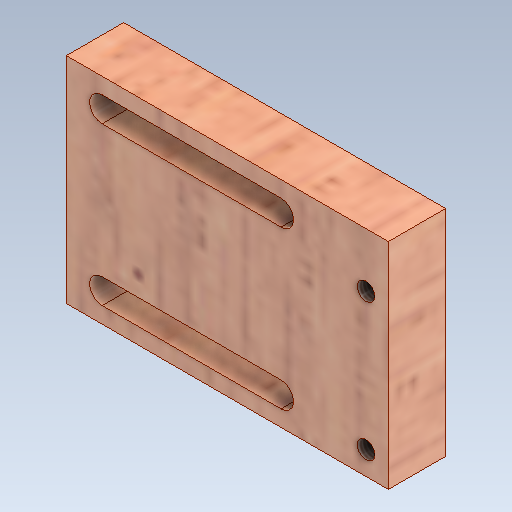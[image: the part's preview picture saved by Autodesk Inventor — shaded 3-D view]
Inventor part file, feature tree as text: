
AUTODESK INVENTOR PART (.ipt)
format: ipt  version: 2020 (Build 240168000, 168)  size: 275,456 bytes
history: native  units: mm
features: sketch x3, other x3, extrude x2, reference x2, hole x1
ambient origin geometry x8: Origin, YZ Plane, XZ Plane, XY Plane, X Axis, Y Axis, Z Axis, Center Point
bodies: Solid1 (feature_tree)
feature tree (11):
  extrude  "Extrusion1"  Depth=30.0mm
  extrude  "Extrusion5"  Depth=3.5mm
  hole  "Hole1"  [1 undecoded]
  sketch  "Sketch1"  dims[d0=45.0mm d1=30.0mm]
  sketch  "Sketch5"  dims[d2=8.0mm d3=0.0mm d29=3.5mm]
  sketch  "Sketch6"  dims[d30=4.0mm d31=4.0mm d33=25.0mm d34=10.0mm d35=0.0mm d36=5.0mm d37=2.459mm d38=8.0mm d39=4.0mm d40=2.0mm d41=90.0deg d42=8.0mm d43=20.594885mm]
  reference  "Reference1"
  reference  "Reference2"
  parser-record x1  (decoder bookkeeping rows leaked as tree rows — omitted from the tree; the rows remain in map.json)
  other  "0005-00-00 Ansamblu_General_V1.iam"
  other  "0005-20-1003 Switch:2"
note: 1 required parameter value undecoded (feature->parameter linkage not recoverable at this tier; creation-order binding heuristic only, values carry confidence <= 0.55)
note: 1 file-system path scrubbed to <path> (originals preserved in map.json)
